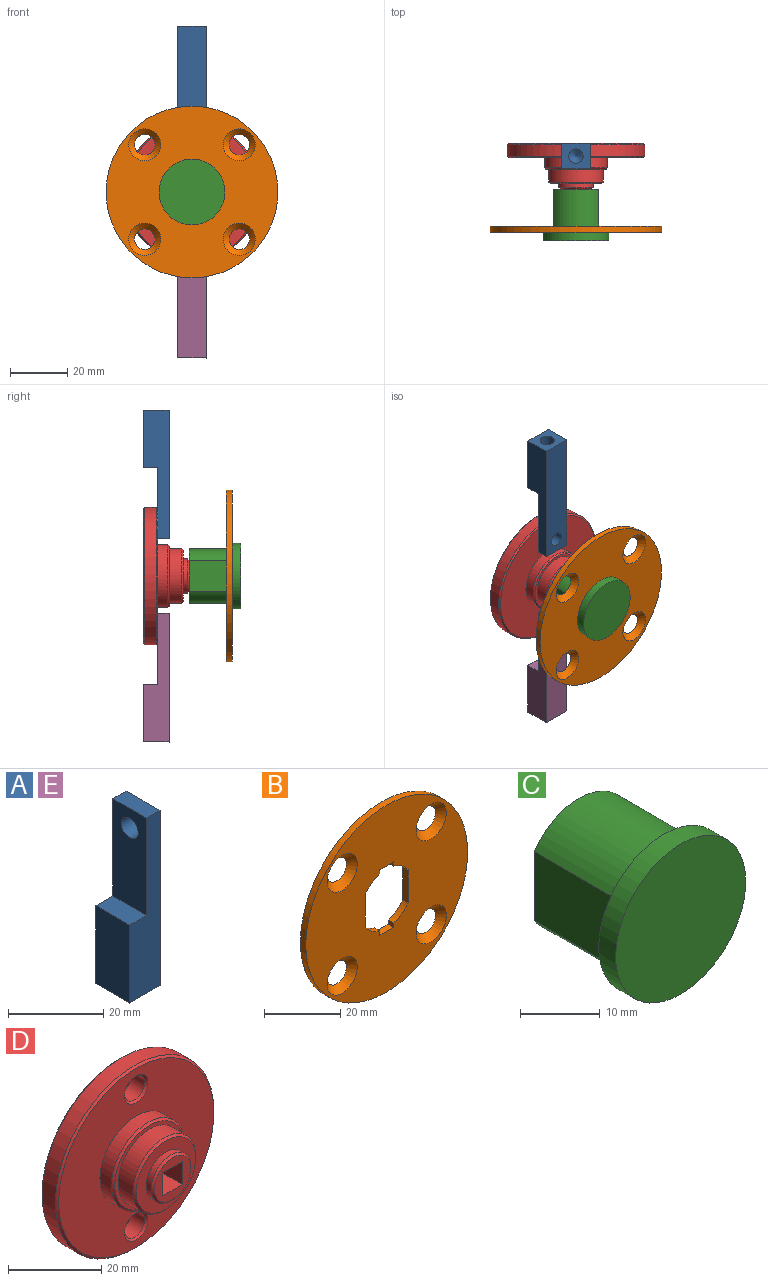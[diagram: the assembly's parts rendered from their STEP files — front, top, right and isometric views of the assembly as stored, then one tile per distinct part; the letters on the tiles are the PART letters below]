
ASSEMBLY  parts=5 mates=3
PART A: 11 faces, bbox 9x10x45 mm
  f0: plane 10x9mm, normal (0,0,-1), area 70.4mm2, adj f1,f5,f6,f7,f9
  f1: plane 45x10mm, normal (1,0,0), area 430.4mm2, adj f0,f2,f6,f7,f10
  f2: plane 10x4mm, normal (0,0,1), area 40mm2, adj f1,f3,f6,f7
  f3: plane 25x10mm, normal (-1,0,0), area 230.4mm2, adj f2,f4,f6,f7,f10
  f4: plane 10x5mm, normal (0,0,1), area 50mm2, adj f3,f5,f6,f7
  f5: plane 20x10mm, normal (-1,0,0), area 200mm2, adj f0,f4,f6,f7
  f6: plane 45x9mm, normal (0,-1,0), area 280mm2, adj f0,f1,f2,f3,f4,f5
  f7: plane 45x9mm, normal (0,1,0), area 280mm2, adj f0,f1,f2,f3,f4,f5
  f8: cone r=0mm half-angle=59deg, axis (0,0,-1), area 22.9mm2, adj f9
  f9: cylinder r=2.5mm len=15mm, axis (0,0,-1), area 235.6mm2, adj f0,f8
  f10: cylinder r=2.5mm len=5mm, axis (-1,0,0), area 62.8mm2, adj f1,f3
PART B: 19 faces, bbox 60x2x60 mm
  f0: plane 60x60mm, normal (0,-1,0), area 2161.6mm2, adj f2,f3,f4,f5,f6,f7,f8,f9
  f1: plane 60x60mm, normal (0,1,0), area 2392.9mm2, adj f2,f3,f4,f5,f6,f7,f8,f9
  f2: cylinder r=9.5mm len=5.4mm, axis (0,-1,0), area 13.6mm2, adj f0,f1,f7,f17
  f3: cylinder r=9.5mm len=5.4mm, axis (0,-1,0), area 13.6mm2, adj f0,f1,f7,f14
  f4: cylinder r=30mm len=60mm, axis (0,1,0), area 377mm2, adj f0,f1
  f5: plane 10.55x2mm, normal (-1,0,0), area 21.1mm2, adj f0,f1,f6,f8
  f6: cylinder r=9.5mm len=5.4mm, axis (0,-1,0), area 13.6mm2, adj f0,f1,f5,f18
  f7: plane 10.55x2mm, normal (1,0,0), area 21.1mm2, adj f0,f1,f2,f3
  f8: cylinder r=9.5mm len=5.4mm, axis (0,-1,0), area 13.6mm2, adj f0,f1,f5,f13
  f9: cone r=2.5mm half-angle=45deg, axis (0,-1,0), area 81.7mm2, adj f0,f1
  f10: cone r=2.5mm half-angle=45deg, axis (0,-1,0), area 81.7mm2, adj f0,f1
  f11: cone r=2.5mm half-angle=45deg, axis (0,-1,0), area 81.7mm2, adj f0,f1
  f12: cone r=2.5mm half-angle=45deg, axis (0,-1,0), area 81.7mm2, adj f0,f1
  f13: plane 2x1.34mm, normal (-1,0,0), area 2.7mm2, adj f0,f1,f8,f15
  f14: plane 2x1.34mm, normal (1,0,0), area 2.7mm2, adj f0,f1,f3,f15
  f15: plane 5x2mm, normal (0,0,1), area 10mm2, adj f0,f1,f13,f14
  f16: plane 5x2mm, normal (0,0,-1), area 10mm2, adj f0,f1,f17,f18
  f17: plane 2x1.34mm, normal (1,0,0), area 2.7mm2, adj f0,f1,f2,f16
  f18: plane 2x1.34mm, normal (-1,0,0), area 2.7mm2, adj f0,f1,f6,f16
PART C: 15 faces, bbox 23x21x23 mm
  f0: cylinder r=9.5mm len=15.8mm, axis (0,1,0), area 279.9mm2, adj f1,f5,f6,f7
  f1: plane 19x15.8mm, normal (0,1,0), area 224.6mm2, adj f0,f2,f6,f7,f8,f9,f10,f11
  f2: cylinder r=9.5mm len=15.8mm, axis (0,1,0), area 279.9mm2, adj f1,f5,f6,f7
  f3: cylinder r=11.5mm len=23mm, axis (0,1,0), area 216.8mm2, adj f4,f5
  f4: plane 23x23mm, normal (0,-1,0), area 415.5mm2, adj f3
  f5: plane 23x23mm, normal (0,1,0), area 154.9mm2, adj f0,f2,f3,f6,f7
  f6: plane 15x10.55mm, normal (-1,0,0), area 158.3mm2, adj f0,f1,f2,f5
  f7: plane 15x10.55mm, normal (1,0,0), area 158.3mm2, adj f0,f1,f2,f5
  f8: plane 6x3mm, normal (1,0,0), area 18mm2, adj f1,f9,f11,f12
  f9: plane 6x3mm, normal (0,0,-1), area 18mm2, adj f1,f8,f10,f12
  f10: plane 6x3mm, normal (-1,0,0), area 18mm2, adj f1,f9,f11,f12
  f11: plane 6x3mm, normal (0,0,1), area 18mm2, adj f1,f8,f10,f12
  f12: plane 6x6mm, normal (0,1,0), area 16.4mm2, adj f8,f9,f10,f11,f14
  f13: cone r=0mm half-angle=59deg, axis (0,1,0), area 22.9mm2, adj f14
  f14: cylinder r=2.5mm len=15mm, axis (0,1,0), area 235.6mm2, adj f12,f13
PART D: 27 faces, bbox 48x16x48 mm
  f0: plane 11x11mm, normal (0,-1,0), area 59mm2, adj f2,f3,f4,f5,f17
  f1: cylinder r=9.5mm len=19mm, axis (0,1,0), area 268.6mm2, adj f18,f25
  f2: plane 6x6mm, normal (1,0,0), area 36mm2, adj f0,f3,f5,f14
  f3: plane 6x6mm, normal (0,0,1), area 36mm2, adj f0,f2,f4,f14
  f4: plane 6x6mm, normal (-1,0,0), area 36mm2, adj f0,f3,f5,f14
  f5: plane 6x6mm, normal (0,0,-1), area 36mm2, adj f0,f2,f4,f14
  f6: plane 47x47mm, normal (0,1,0), area 1523mm2, adj f11,f19,f20,f21
  f7: cylinder r=24mm len=48mm, axis (0,1,0), area 603.2mm2, adj f11,f12
  f8: plane 47x47mm, normal (0,-1,0), area 1275.6mm2, adj f12,f22,f23,f24
  f9: cylinder r=3.05mm len=6.1mm, axis (0,1,0), area 76.7mm2, adj f20,f22
  f10: cylinder r=3.05mm len=6.1mm, axis (0,1,0), area 76.7mm2, adj f21,f23
  f11: cone r=24mm half-angle=45deg, axis (0,-1,0), area 105.5mm2, adj f6,f7
  f12: cone r=23.5mm half-angle=45deg, axis (0,1,0), area 105.5mm2, adj f7,f8
  f13: cylinder r=6mm len=12mm, axis (0,1,0), area 358.1mm2, adj f14,f19
  f14: plane 12x12mm, normal (0,1,0), area 77.1mm2, adj f2,f3,f4,f5,f13
  f15: cylinder r=6mm len=12mm, axis (0,-1,0), area 56.5mm2, adj f16,f17
  f16: plane 18x18mm, normal (0,-1,0), area 141.4mm2, adj f15,f18
  f17: cone r=5.5mm half-angle=45deg, axis (0,1,0), area 25.5mm2, adj f0,f15
  f18: cone r=9mm half-angle=45deg, axis (0,1,0), area 41.1mm2, adj f1,f16
  f19: cone r=6mm half-angle=45deg, axis (0,1,0), area 27.8mm2, adj f6,f13
  f20: cone r=3.05mm half-angle=45deg, axis (0,1,0), area 14.7mm2, adj f6,f9
  f21: cone r=3.05mm half-angle=45deg, axis (0,1,0), area 14.7mm2, adj f6,f10
  f22: cone r=3.55mm half-angle=45deg, axis (0,-1,0), area 14.7mm2, adj f8,f9
  f23: cone r=3.55mm half-angle=45deg, axis (0,-1,0), area 14.7mm2, adj f8,f10
  f24: cylinder r=11mm len=22mm, axis (0,1,0), area 241.9mm2, adj f8,f26
  f25: plane 21x21mm, normal (0,-1,0), area 62.8mm2, adj f1,f26
  f26: cone r=10.5mm half-angle=45deg, axis (0,1,0), area 47.8mm2, adj f24,f25
PART E: same geometry as A
PLACE A rot(axis=(-0.71,0.71,0),180deg) t=(-6.26,-0.96,40.99)mm
PLACE B t=(-1.26,-20.96,2.99)mm
PLACE C t=(-1.26,-7.96,2.99)mm
PLACE D t=(-1.26,8.04,2.99)mm
PLACE E rot(axis=(0,0,-1),90deg) t=(3.74,-0.96,-35.01)mm
MATE fastened E.f10 <-> D.f9  axis (0,1,0) through (-1.26,3.04,-15.01)mm
MATE fastened D.f13 <-> C.f0  axis (0,-1,0) through (-1.26,-7.96,2.99)mm
MATE fastened B.f4 <-> C.f3  axis (0,-1,0) through (-1.26,-22.96,2.99)mm
